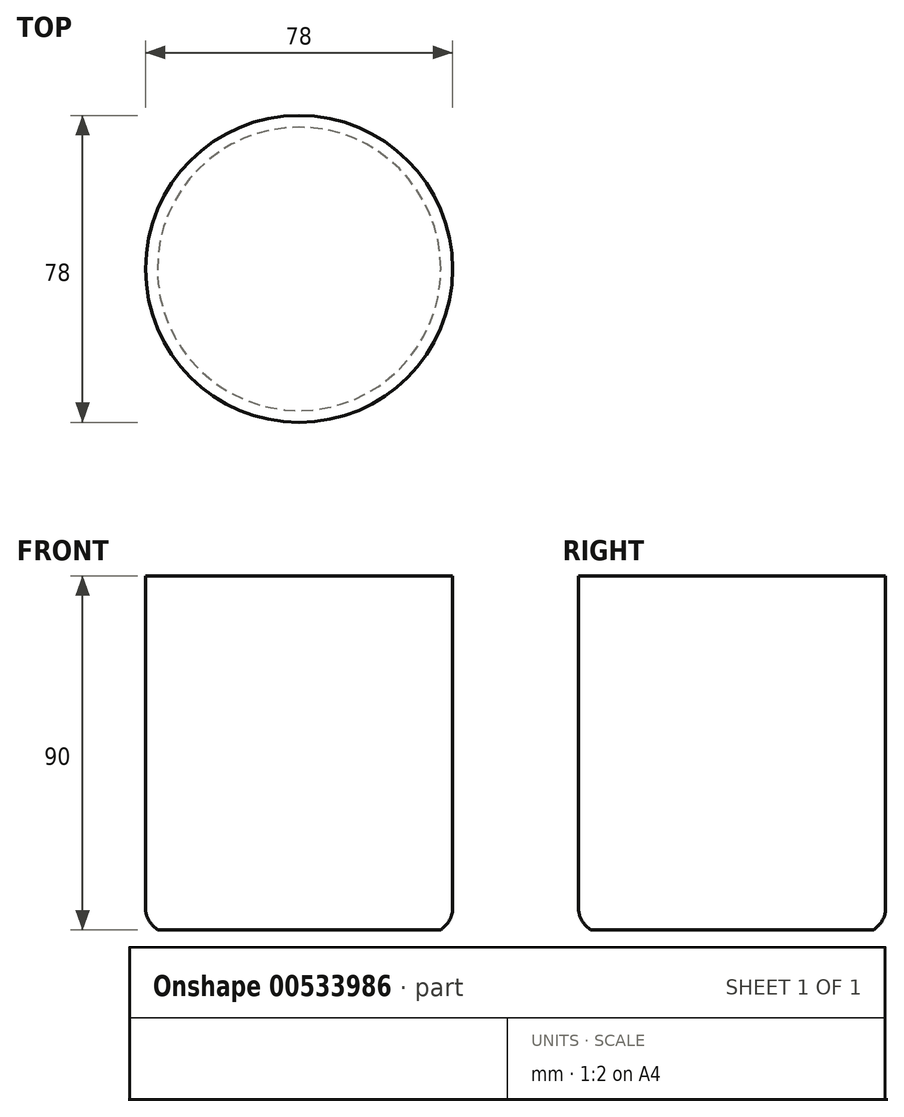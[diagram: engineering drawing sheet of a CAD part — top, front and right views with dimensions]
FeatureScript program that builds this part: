
annotation { "Feature Type Name" : "Feature", "Feature Type Description" : "" }
export const myFeature = defineFeature(function(context is Context, id is Id, definition is map)
    precondition{}
    {
        {
            var Q0;
            Q0=qCreatedBy(makeId("Top.planeOp"),FACE);
            var sketch = newSketch(context, id + "F0", { "sketchPlane" : qUnion([Q0])});
            skCircle(sketch, "E0", {"center": v(0, 0) * mm, "radius": 39 * mm});
            skSolve(sketch);
        }
        {
            var Q0;
            Q0 = qSketchRegion(id + "F0", true);
            extrude(context, id + "F1", {"entities" : qUnion([Q0]), "depth" : 90 * mm, "offsetDistance" : 25 * mm});
        }
        {
            var Q0;
            Q0=makeQuery(id+"F1.opExtrude","CAP_EDGE",EDGE,{"disambiguationData":[OSD([sQuery(id+"F0.wireOp",EDGE,"E0")])],"isStart":true});
            chamfer(context, id + "F2", {"entities" : qUnion([Q0]), "width" : 3 * mm, "tangentPropagation" : true});
        }
        {
            var Q0;
            {var subQ0=sQuery(id+"F0.wireOp",EDGE,"E0");Q0=makeQuery(id+"F2.opChamfer","BLEND_EDGE",EDGE,{"blendedFrom":[makeQuery(id+"F1.opExtrude","CAP_EDGE",EDGE,{"disambiguationData":[OSD([subQ0])],"isStart":true}),makeQuery(id+"F1.opExtrude","SWEPT_FACE",FACE,{"disambiguationData":[OSD([subQ0])]})],"blendedInto":[makeQuery(id+"F1.opExtrude","SWEPT_FACE",FACE,{"disambiguationData":[OSD([subQ0])]})]});}
            fillet(context, id + "F3", {"entities" : qUnion([Q0]), "radius" : 6 * mm, "tangentPropagation" : true, "allowEdgeOverflow" : false});
        }
    });
